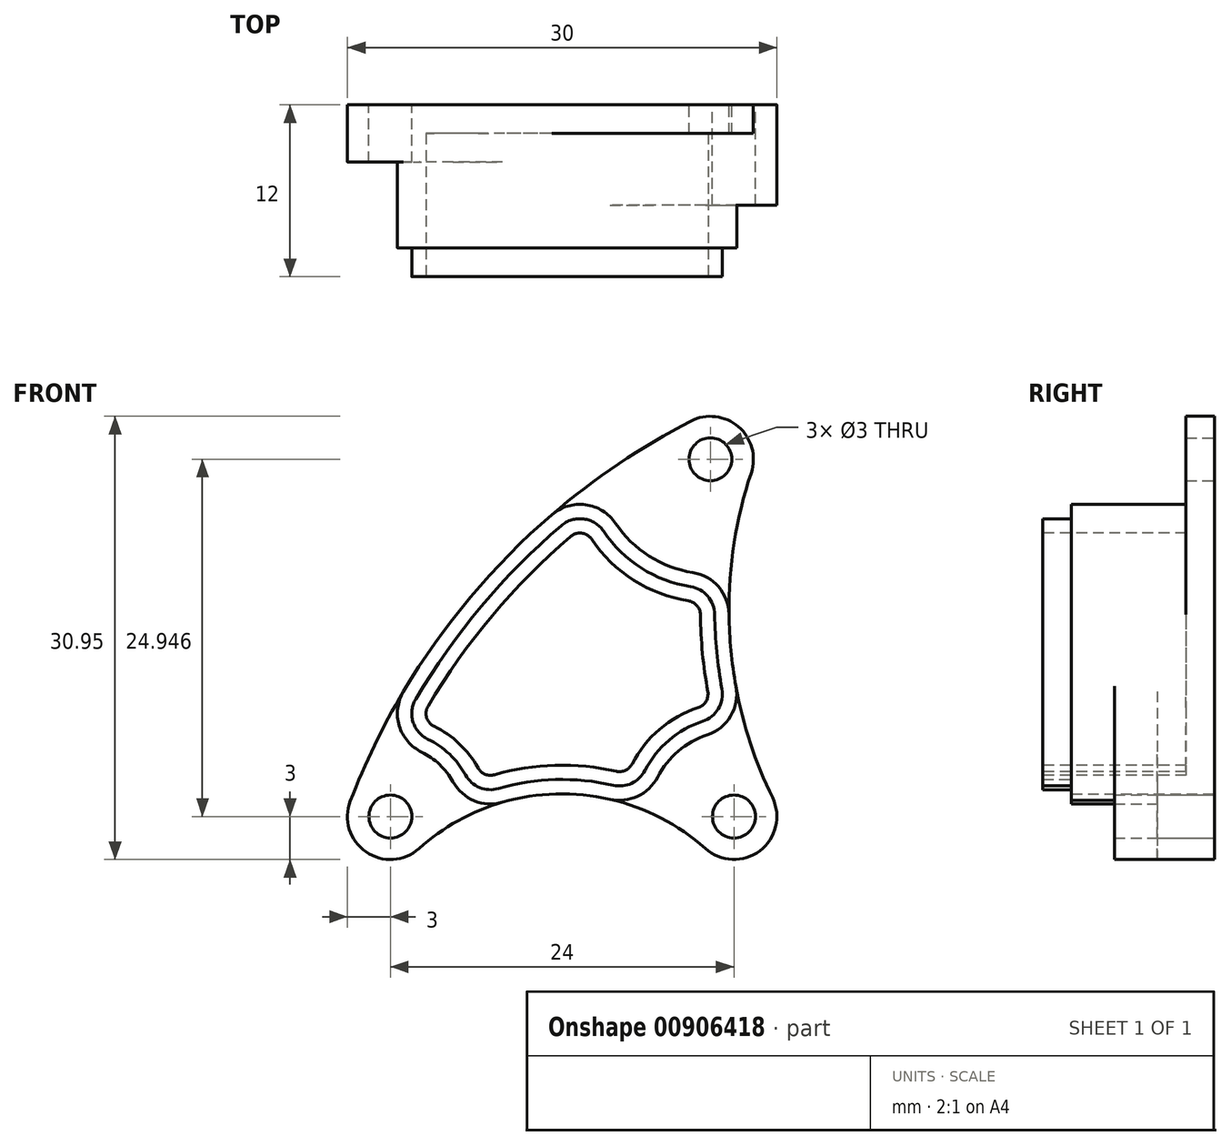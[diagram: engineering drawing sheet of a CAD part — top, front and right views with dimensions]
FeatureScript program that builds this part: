
annotation { "Feature Type Name" : "Feature", "Feature Type Description" : "" }
export const myFeature = defineFeature(function(context is Context, id is Id, definition is map)
    precondition{}
    {
        {
            var Q0;
            Q0=qCreatedBy(makeId("Front.planeOp"),FACE);
            var sketch = newSketch(context, id + "F0", { "sketchPlane" : qUnion([Q0])});
            skArc(sketch, "E0", {"start": v(-2.8, 1.07) * mm, "mid": v(-1.7, -2.47) * mm, "end": v(2, -2.24) * mm});
            skArc(sketch, "E1", {"start": v(25.2, 24) * mm, "mid": v(24.31, 27.22) * mm, "end": v(20.99, 27.61) * mm});
            skArc(sketch, "E2", {"start": v(22, -2.24) * mm, "mid": v(25.8, -2.4) * mm, "end": v(26.7, 1.32) * mm});
            skArc(sketch, "E3", {"start": v(20.99, 27.61) * mm, "mid": v(6.65, 16.54) * mm, "end": v(-2.8, 1.07) * mm});
            skArc(sketch, "E4", {"start": v(22, -2.24) * mm, "mid": v(12, 1.58) * mm, "end": v(2, -2.24) * mm});
            skArc(sketch, "E5", {"start": v(25.2, 24) * mm, "mid": v(23.72, 12.5) * mm, "end": v(26.7, 1.32) * mm});
            skSolve(sketch);
        }
        {
            var Q0;
            Q0=makeQuery(id+"F0.imprint","IMPRINT",FACE,{"disambiguationData":[TD([[makeQuery(id+"F0.imprint","IMPRINT",EDGE,{"derivedFrom":sQuery(id+"F0.wireOp",EDGE,"E0")}),1.0]])]});
            extrude(context, id + "F1", {"entities" : qUnion([Q0]), "depth" : 2 * mm, "offsetDistance" : 25 * mm});
        }
        {
            var Q0;
            Q0=makeQuery(id+"F1.opExtrude","CAP_FACE",FACE,{"disambiguationData":[OSD([sQuery(id+"F0.wireOp",EDGE,"E0"),sQuery(id+"F0.wireOp",EDGE,"E1"),sQuery(id+"F0.wireOp",EDGE,"E2"),sQuery(id+"F0.wireOp",EDGE,"E3"),sQuery(id+"F0.wireOp",EDGE,"E4"),sQuery(id+"F0.wireOp",EDGE,"E5")])],"isStart":false});
            var sketch = newSketch(context, id + "F2", { "sketchPlane" : qUnion([Q0])});
            skArc(sketch, "E6", {"start": v(4.37, 2.42) * mm, "mid": v(3.44, 3.63) * mm, "end": v(2.18, 4.5) * mm});
            skArc(sketch, "E7", {"start": v(22.13, 5.7) * mm, "mid": v(20.1, 4.57) * mm, "end": v(18.67, 2.75) * mm});
            skArc(sketch, "E8", {"start": v(15.72, 20.48) * mm, "mid": v(18.06, 18.2) * mm, "end": v(21.12, 17.04) * mm});
            skArc(sketch, "E9.0", {"start": v(11.28, 21.07) * mm, "mid": v(5.6, 15.32) * mm, "end": v(0.91, 8.73) * mm});
            skArc(sketch, "E10.0", {"start": v(23.66, 14.11) * mm, "mid": v(23.8, 11.6) * mm, "end": v(24.14, 9.09) * mm});
            skArc(sketch, "E11.0", {"start": v(15.34, 1.2) * mm, "mid": v(11.57, 1.58) * mm, "end": v(7.83, 1) * mm});
            skPoint(sketch, "E12.newPointA", {"position": v(-2.8, 1.07) * mm});
            skArc(sketch, "E12.filletArc", {"start": v(0.91, 8.73) * mm, "mid": v(0.62, 6.34) * mm, "end": v(2.18, 4.5) * mm});
            skPoint(sketch, "E13.newPointB", {"position": v(20.99, 27.61) * mm});
            skArc(sketch, "E13.filletArc", {"start": v(15.72, 20.48) * mm, "mid": v(13.64, 21.77) * mm, "end": v(11.28, 21.07) * mm});
            skPoint(sketch, "E14.newPointB", {"position": v(25.2, 24) * mm});
            skArc(sketch, "E14.filletArc", {"start": v(23.66, 14.11) * mm, "mid": v(22.92, 16.04) * mm, "end": v(21.12, 17.04) * mm});
            skPoint(sketch, "E15.newPointA", {"position": v(26.7, 1.32) * mm});
            skArc(sketch, "E15.filletArc", {"start": v(22.13, 5.7) * mm, "mid": v(23.77, 7.02) * mm, "end": v(24.14, 9.09) * mm});
            skPoint(sketch, "E16.newPointB", {"position": v(22, -2.24) * mm});
            skArc(sketch, "E16.filletArc", {"start": v(15.34, 1.2) * mm, "mid": v(17.27, 1.41) * mm, "end": v(18.67, 2.75) * mm});
            skPoint(sketch, "E17.newPointA", {"position": v(2, -2.24) * mm});
            skArc(sketch, "E17.filletArc", {"start": v(4.37, 2.42) * mm, "mid": v(5.85, 1.1) * mm, "end": v(7.83, 1) * mm});
            skSolve(sketch);
        }
        {
            var Q0;
            Q0=makeQuery(id+"F2.imprint","IMPRINT",FACE,{"disambiguationData":[TD([[makeQuery(id+"F2.imprint","IMPRINT",EDGE,{"derivedFrom":sQuery(id+"F2.wireOp",EDGE,"E6")}),-1.0]])]});
            extrude(context, id + "F3", {"entities" : qUnion([Q0]), "operationType" : NewBodyOperationType.ADD, "depth" : 8 * mm, "offsetDistance" : 25 * mm});
        }
        {
            var Q0;
            {var subQ0=sQuery(id+"F0.wireOp",EDGE,"E4");var subQ1=sQuery(id+"F0.wireOp",EDGE,"E3");var subQ2=sQuery(id+"F0.wireOp",EDGE,"E0");Q0=makeQuery(id+"F3.boolean.opBoolean","SPLIT",FACE,{"disambiguationData":[TD([makeQuery(id+"F1.opExtrude","SWEPT_FACE",FACE,{"disambiguationData":[OSD([subQ2])]})])],"derivedFrom":makeQuery(id+"F1.opExtrude","CAP_FACE",FACE,{"disambiguationData":[OSD([subQ2,sQuery(id+"F0.wireOp",EDGE,"E1"),sQuery(id+"F0.wireOp",EDGE,"E2"),subQ1,subQ0,sQuery(id+"F0.wireOp",EDGE,"E5")])],"isStart":false})});}
            var sketch = newSketch(context, id + "F4", { "sketchPlane" : qUnion([Q0])});
            skArc(sketch, "E18.0.0", {"start": v(7.83, 1) * mm, "mid": v(5.85, 1.1) * mm, "end": v(4.37, 2.42) * mm});
            skArc(sketch, "E18.0.1", {"start": v(4.37, 2.42) * mm, "mid": v(3.44, 3.63) * mm, "end": v(2.18, 4.5) * mm});
            skArc(sketch, "E18.0.2", {"start": v(2.18, 4.5) * mm, "mid": v(0.62, 6.34) * mm, "end": v(0.91, 8.73) * mm});
            skArc(sketch, "E18.0.3", {"start": v(0.91, 8.73) * mm, "mid": v(-1.1, 4.98) * mm, "end": v(-2.8, 1.07) * mm});
            skArc(sketch, "E18.0.4", {"start": v(-2.8, 1.07) * mm, "mid": v(-1.7, -2.47) * mm, "end": v(2, -2.24) * mm});
            skArc(sketch, "E18.0.5", {"start": v(2, -2.24) * mm, "mid": v(4.73, -0.3) * mm, "end": v(7.83, 1) * mm});
            skSolve(sketch);
        }
        {
            var Q0;
            Q0=makeQuery(id+"F4.imprint","IMPRINT",FACE,{"disambiguationData":[TD([[makeQuery(id+"F4.imprint","IMPRINT",EDGE,{"derivedFrom":sQuery(id+"F4.wireOp",EDGE,"E18.0.0")}),-1.0]])]});
            extrude(context, id + "F5", {"entities" : qUnion([Q0]), "operationType" : NewBodyOperationType.ADD, "depth" : 2 * mm, "offsetDistance" : 25 * mm});
        }
        {
            var Q0;
            {var subQ0=sQuery(id+"F0.wireOp",EDGE,"E5");var subQ1=sQuery(id+"F0.wireOp",EDGE,"E2");var subQ2=sQuery(id+"F0.wireOp",EDGE,"E4");Q0=makeQuery(id+"F3.boolean.opBoolean","SPLIT",FACE,{"disambiguationData":[TD([makeQuery(id+"F1.opExtrude","SWEPT_FACE",FACE,{"disambiguationData":[OSD([subQ1])]})])],"derivedFrom":makeQuery(id+"F1.opExtrude","CAP_FACE",FACE,{"disambiguationData":[OSD([sQuery(id+"F0.wireOp",EDGE,"E0"),sQuery(id+"F0.wireOp",EDGE,"E1"),subQ1,sQuery(id+"F0.wireOp",EDGE,"E3"),subQ2,subQ0])],"isStart":false})});}
            var sketch = newSketch(context, id + "F6", { "sketchPlane" : qUnion([Q0])});
            skArc(sketch, "E19.0.0", {"start": v(24.14, 9.09) * mm, "mid": v(23.77, 7.02) * mm, "end": v(22.13, 5.7) * mm});
            skArc(sketch, "E19.0.1", {"start": v(22.13, 5.7) * mm, "mid": v(20.1, 4.57) * mm, "end": v(18.67, 2.75) * mm});
            skArc(sketch, "E19.0.2", {"start": v(18.67, 2.75) * mm, "mid": v(17.27, 1.41) * mm, "end": v(15.34, 1.2) * mm});
            skArc(sketch, "E19.0.3", {"start": v(15.34, 1.2) * mm, "mid": v(18.89, -0.1) * mm, "end": v(22, -2.24) * mm});
            skArc(sketch, "E19.0.4", {"start": v(22, -2.24) * mm, "mid": v(25.8, -2.4) * mm, "end": v(26.7, 1.32) * mm});
            skArc(sketch, "E19.0.5", {"start": v(26.7, 1.32) * mm, "mid": v(25.15, 5.12) * mm, "end": v(24.14, 9.09) * mm});
            skSolve(sketch);
        }
        {
            var Q0;
            Q0=makeQuery(id+"F6.imprint","IMPRINT",FACE,{"disambiguationData":[TD([[makeQuery(id+"F6.imprint","IMPRINT",EDGE,{"derivedFrom":sQuery(id+"F6.wireOp",EDGE,"E19.0.0")}),-1.0]])]});
            extrude(context, id + "F7", {"entities" : qUnion([Q0]), "operationType" : NewBodyOperationType.ADD, "depth" : 5 * mm, "offsetDistance" : 25 * mm});
        }
        {
            var Q0;
            Q0=makeQuery(id+"F3.opExtrude","CAP_FACE",FACE,{"disambiguationData":[OSD([sQuery(id+"F2.wireOp",EDGE,"E6"),sQuery(id+"F2.wireOp",EDGE,"E7"),sQuery(id+"F2.wireOp",EDGE,"E8"),sQuery(id+"F2.wireOp",EDGE,"E9.0"),sQuery(id+"F2.wireOp",EDGE,"E10.0"),sQuery(id+"F2.wireOp",EDGE,"E11.0"),sQuery(id+"F2.wireOp",EDGE,"E12.filletArc"),sQuery(id+"F2.wireOp",EDGE,"E13.filletArc"),sQuery(id+"F2.wireOp",EDGE,"E14.filletArc"),sQuery(id+"F2.wireOp",EDGE,"E15.filletArc"),sQuery(id+"F2.wireOp",EDGE,"E16.filletArc"),sQuery(id+"F2.wireOp",EDGE,"E17.filletArc")])],"isStart":false});
            var sketch = newSketch(context, id + "F8", { "sketchPlane" : qUnion([Q0])});
            skArc(sketch, "E20.0", {"start": v(21.82, 6.65) * mm, "mid": v(22.91, 7.53) * mm, "end": v(23.16, 8.9) * mm});
            skArc(sketch, "E20.1", {"start": v(11.93, 20.32) * mm, "mid": v(6.36, 14.68) * mm, "end": v(1.77, 8.22) * mm});
            skArc(sketch, "E20.2", {"start": v(14.9, 19.92) * mm, "mid": v(13.5, 20.78) * mm, "end": v(11.93, 20.32) * mm});
            skArc(sketch, "E20.3", {"start": v(20.97, 16.05) * mm, "mid": v(17.53, 17.35) * mm, "end": v(14.9, 19.92) * mm});
            skArc(sketch, "E20.4", {"start": v(22.66, 14.1) * mm, "mid": v(22.17, 15.39) * mm, "end": v(20.97, 16.05) * mm});
            skArc(sketch, "E20.5", {"start": v(1.77, 8.22) * mm, "mid": v(1.58, 6.62) * mm, "end": v(2.62, 5.4) * mm});
            skArc(sketch, "E20.6", {"start": v(23.16, 8.9) * mm, "mid": v(22.8, 11.5) * mm, "end": v(22.66, 14.1) * mm});
            skArc(sketch, "E20.7", {"start": v(2.62, 5.4) * mm, "mid": v(4.13, 4.36) * mm, "end": v(5.25, 2.9) * mm});
            skArc(sketch, "E20.8", {"start": v(5.25, 2.9) * mm, "mid": v(6.24, 2.03) * mm, "end": v(7.55, 1.95) * mm});
            skArc(sketch, "E20.9", {"start": v(7.55, 1.95) * mm, "mid": v(11.54, 2.58) * mm, "end": v(15.56, 2.18) * mm});
            skArc(sketch, "E20.10", {"start": v(15.56, 2.18) * mm, "mid": v(16.85, 2.32) * mm, "end": v(17.78, 3.21) * mm});
            skArc(sketch, "E20.11", {"start": v(17.78, 3.21) * mm, "mid": v(19.46, 5.33) * mm, "end": v(21.82, 6.65) * mm});
            skSolve(sketch);
        }
        {
            var Q0;
            Q0=makeQuery(id+"F8.imprint","IMPRINT",FACE,{"disambiguationData":[TD([[makeQuery(id+"F8.imprint","IMPRINT",EDGE,{"derivedFrom":sQuery(id+"F8.wireOp",EDGE,"E20.0")}),1.0]])]});
            extrude(context, id + "F9", {"entities" : qUnion([Q0]), "operationType" : NewBodyOperationType.ADD, "depth" : 2 * mm, "offsetDistance" : 25 * mm});
        }
        {
            var Q0;
            Q0=makeQuery(id+"F9.opExtrude","CAP_FACE",FACE,{"disambiguationData":[OSD([sQuery(id+"F8.wireOp",EDGE,"E20.0"),sQuery(id+"F8.wireOp",EDGE,"E20.1"),sQuery(id+"F8.wireOp",EDGE,"E20.2"),sQuery(id+"F8.wireOp",EDGE,"E20.3"),sQuery(id+"F8.wireOp",EDGE,"E20.4"),sQuery(id+"F8.wireOp",EDGE,"E20.5"),sQuery(id+"F8.wireOp",EDGE,"E20.6"),sQuery(id+"F8.wireOp",EDGE,"E20.7"),sQuery(id+"F8.wireOp",EDGE,"E20.8"),sQuery(id+"F8.wireOp",EDGE,"E20.9"),sQuery(id+"F8.wireOp",EDGE,"E20.10"),sQuery(id+"F8.wireOp",EDGE,"E20.11")])],"isStart":false});
            var sketch = newSketch(context, id + "F10", { "sketchPlane" : qUnion([Q0])});
            skArc(sketch, "E21.0", {"start": v(12.58, 19.56) * mm, "mid": v(7.13, 14.04) * mm, "end": v(2.63, 7.7) * mm});
            skArc(sketch, "E21.1", {"start": v(15.78, 3.16) * mm, "mid": v(16.43, 3.23) * mm, "end": v(16.9, 3.67) * mm});
            skArc(sketch, "E21.2", {"start": v(7.28, 2.91) * mm, "mid": v(11.51, 3.58) * mm, "end": v(15.78, 3.16) * mm});
            skArc(sketch, "E21.3", {"start": v(6.12, 3.4) * mm, "mid": v(6.62, 2.95) * mm, "end": v(7.28, 2.91) * mm});
            skArc(sketch, "E21.4", {"start": v(3.05, 6.3) * mm, "mid": v(4.81, 5.08) * mm, "end": v(6.12, 3.4) * mm});
            skArc(sketch, "E21.5", {"start": v(16.9, 3.67) * mm, "mid": v(18.81, 6.09) * mm, "end": v(21.5, 7.6) * mm});
            skArc(sketch, "E21.6", {"start": v(2.63, 7.7) * mm, "mid": v(2.53, 6.91) * mm, "end": v(3.05, 6.3) * mm});
            skArc(sketch, "E21.7", {"start": v(21.5, 7.6) * mm, "mid": v(22.05, 8.04) * mm, "end": v(22.18, 8.73) * mm});
            skArc(sketch, "E21.8", {"start": v(22.18, 8.73) * mm, "mid": v(21.8, 11.4) * mm, "end": v(21.66, 14.1) * mm});
            skArc(sketch, "E21.9", {"start": v(21.66, 14.1) * mm, "mid": v(21.41, 14.73) * mm, "end": v(20.81, 15.07) * mm});
            skArc(sketch, "E21.10", {"start": v(20.81, 15.07) * mm, "mid": v(17, 16.5) * mm, "end": v(14.07, 19.36) * mm});
            skArc(sketch, "E21.11", {"start": v(14.07, 19.36) * mm, "mid": v(13.37, 19.8) * mm, "end": v(12.58, 19.56) * mm});
            skSolve(sketch);
        }
        {
            var Q0;
            Q0=makeQuery(id+"F10.imprint","IMPRINT",FACE,{"disambiguationData":[TD([[makeQuery(id+"F10.imprint","IMPRINT",EDGE,{"derivedFrom":sQuery(id+"F10.wireOp",EDGE,"E21.0")}),1.0]])]});
            extrude(context, id + "F11", {"entities" : qUnion([Q0]), "operationType" : NewBodyOperationType.REMOVE, "oppositeDirection" : true, "depth" : 10 * mm, "offsetDistance" : 25 * mm});
        }
        {
            var Q0;
            Q0=qCreatedBy(makeId("Front.planeOp"),FACE);
            var sketch = newSketch(context, id + "F12", { "sketchPlane" : qUnion([Q0])});
            skCircle(sketch, "E22", {"center": v(0, 0) * mm, "radius": 1.5 * mm});
            skCircle(sketch, "E23", {"center": v(22.36, 24.95) * mm, "radius": 1.5 * mm});
            skCircle(sketch, "E24", {"center": v(24, 0) * mm, "radius": 1.5 * mm});
            skSolve(sketch);
        }
        {
            var Q0;
            Q0=qSketchRegion(id+"F12",true);
            extrude(context, id + "F13", {"entities" : qUnion([Q0]), "operationType" : NewBodyOperationType.REMOVE, "endBound" : BoundingType.THROUGH_ALL, "depth" : 25 * mm, "offsetDistance" : 25 * mm});
        }
    });
